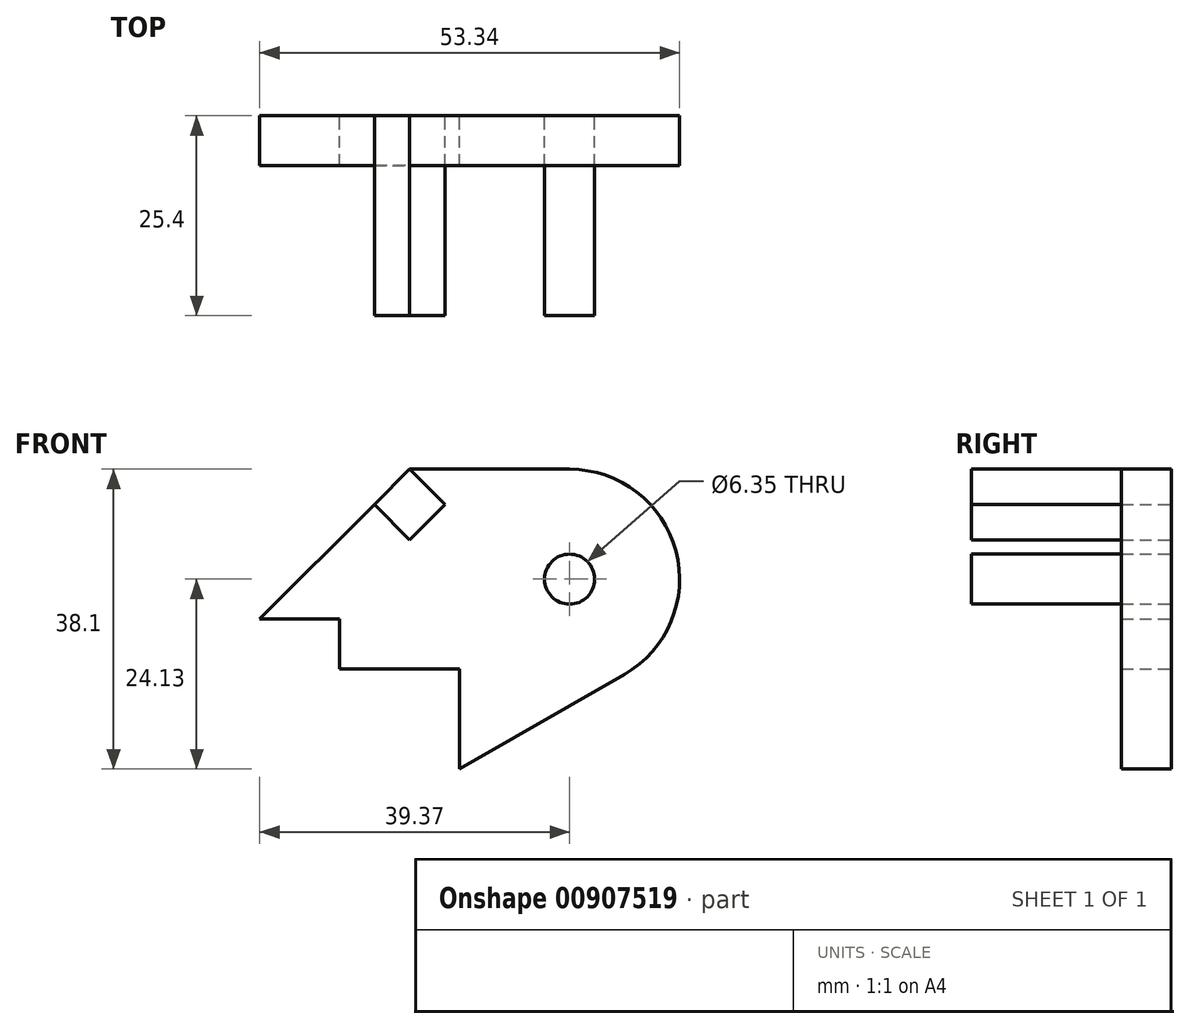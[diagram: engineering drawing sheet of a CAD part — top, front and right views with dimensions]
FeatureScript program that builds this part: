
annotation { "Feature Type Name" : "Feature", "Feature Type Description" : "" }
export const myFeature = defineFeature(function(context is Context, id is Id, definition is map)
    precondition{}
    {
        {
            var Q0;
            Q0=qCreatedBy(makeId("Front.planeOp"),FACE);
            var sketch = newSketch(context, id + "F0", { "sketchPlane" : qUnion([Q0])});
            skLineSegment(sketch, "E0", {"start": v(0, 0) * mm, "end": v(-15.24, 0) * mm});
            skLineSegment(sketch, "E1", {"start": v(-15.24, 0) * mm, "end": v(-15.24, 6.35) * mm});
            skLineSegment(sketch, "E2", {"start": v(-15.24, 6.35) * mm, "end": v(-25.4, 6.35) * mm});
            skLineSegment(sketch, "E3", {"start": v(-25.4, 6.35) * mm, "end": v(-10.84, 20.9) * mm});
            skLineSegment(sketch, "E4", {"start": v(-6.35, 25.4) * mm, "end": v(13.97, 25.4) * mm});
            skArc(sketch, "E5", {"start": v(20.93, -0.69) * mm, "mid": v(27.47, 15.03) * mm, "end": v(13.97, 25.4) * mm});
            skLineSegment(sketch, "E6", {"start": v(20.93, -0.69) * mm, "end": v(0, -12.7) * mm});
            skLineSegment(sketch, "E7", {"start": v(0, -12.7) * mm, "end": v(0, 0) * mm});
            skCircle(sketch, "E8", {"center": v(13.97, 11.43) * mm, "radius": 3.18 * mm});
            skLineSegment(sketch, "E9", {"start": v(-10.84, 20.9) * mm, "end": v(-6.35, 16.42) * mm});
            skLineSegment(sketch, "E10", {"start": v(-6.35, 16.42) * mm, "end": v(-1.86, 20.9) * mm});
            skLineSegment(sketch, "E11", {"start": v(-1.86, 20.9) * mm, "end": v(-6.35, 25.4) * mm});
            skSolve(sketch);
        }
        {
            var Q0;
            Q0 = qSketchRegion(id + "F0", true);
            extrude(context, id + "F1", {"entities" : qUnion([Q0]), "depth" : 6.35 * mm, "offsetDistance" : 25.4 * mm});
        }
        {
            var Q0;
            Q0=qCreatedBy(makeId("Front.planeOp"),FACE);
            var sketch = newSketch(context, id + "F2", { "sketchPlane" : qUnion([Q0])});
            skCircle(sketch, "E12", {"center": v(13.97, 11.43) * mm, "radius": 3.18 * mm});
            skSolve(sketch);
        }
        {
            var Q0;
            Q0 = qSketchRegion(id + "F2", true);
            extrude(context, id + "F3", {"entities" : qUnion([Q0]), "depth" : 25.4 * mm, "offsetDistance" : 25.4 * mm});
        }
        {
            var Q0;
            Q0=qCreatedBy(makeId("Front.planeOp"),FACE);
            var sketch = newSketch(context, id + "F4", { "sketchPlane" : qUnion([Q0])});
            skLineSegment(sketch, "E13", {"start": v(-6.35, 16.42) * mm, "end": v(-1.86, 20.9) * mm});
            skLineSegment(sketch, "E14", {"start": v(-1.86, 20.9) * mm, "end": v(-6.35, 25.4) * mm});
            skLineSegment(sketch, "E15", {"start": v(-6.35, 25.4) * mm, "end": v(-10.84, 20.9) * mm});
            skLineSegment(sketch, "E16", {"start": v(-10.84, 20.9) * mm, "end": v(-6.35, 16.42) * mm});
            skSolve(sketch);
        }
        {
            var Q0;
            Q0 = qSketchRegion(id + "F4", true);
            extrude(context, id + "F5", {"entities" : qUnion([Q0]), "depth" : 25.4 * mm, "offsetDistance" : 25.4 * mm});
        }
    });
